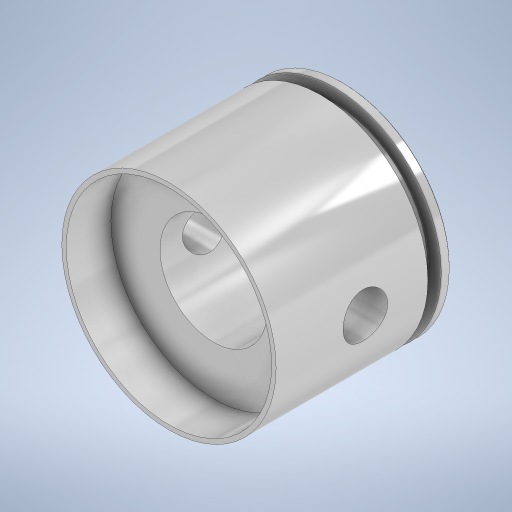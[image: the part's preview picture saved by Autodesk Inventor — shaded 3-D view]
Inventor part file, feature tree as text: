
AUTODESK INVENTOR PART (.ipt)
format: ipt  version: 2024 (Build 280153000, 153)  size: 312,320 bytes
history: native  units: mm
features: sketch x3, hole x2, plane x2, revolve x1, chamfer x1
ambient origin geometry x8: Origin, YZ Plane, XZ Plane, XY Plane, X Axis, Y Axis, Z Axis, Center Point
bodies: Volumenkörper1 (feature_tree)
feature tree (9):
  revolve  "Umdrehung1"
  hole  "Bohrung1"  [1 undecoded]
  plane  "Arbeitsebene2"
  plane  "Arbeitsebene4"
  hole  "Bohrung3"  [1 undecoded]
  chamfer  "Fasen1"  Angle=90.0deg  [1 undecoded]
  sketch  "Skizze1"  dims[d0=24.0mm d1=1.0mm]
  sketch  "Skizze3"  dims[d2=1.5mm d3=19.5mm]
  sketch  "Skizze7"  dims[d4=21.0mm d5=90.0deg d6=12.0mm d7=6.0mm d8=23.0mm d9=5.0mm d10=90.0deg d11=16.0mm d12=0.0mm d14=12.0mm d24=12.0mm d25=10.0mm d26=5.0mm d27=6.0mm d28=4.0mm d29=2.0mm d30=90.0deg d31=8.0mm d32=0.0mm d34=0.1mm d35=2.0mm d36=45.0deg]
note: 3 required parameter values undecoded (feature->parameter linkage not recoverable at this tier; creation-order binding heuristic only, values carry confidence <= 0.55)
